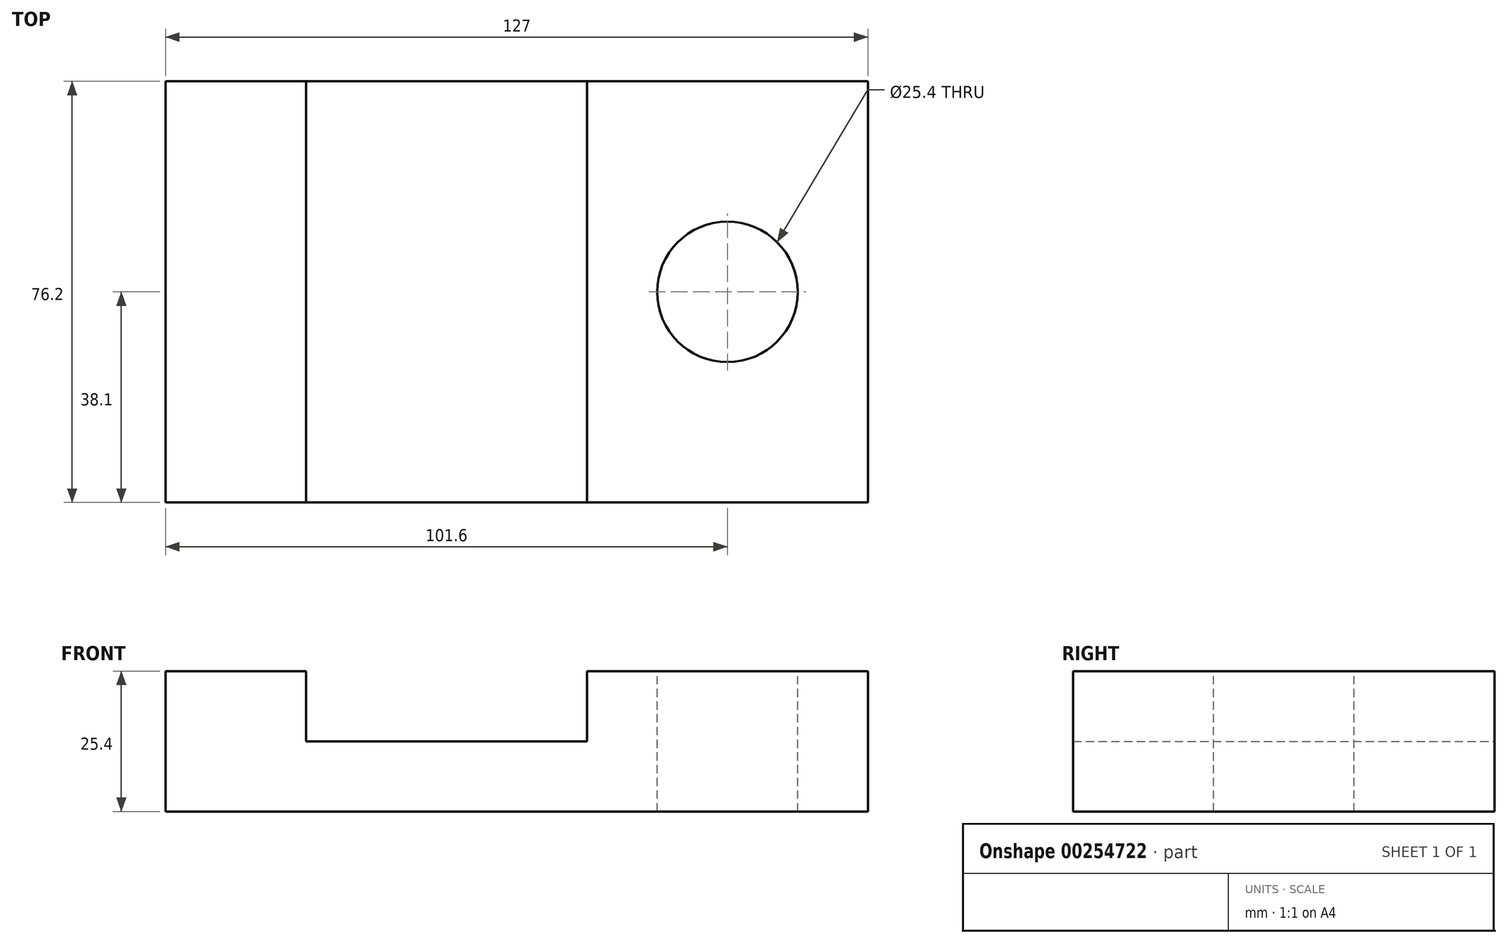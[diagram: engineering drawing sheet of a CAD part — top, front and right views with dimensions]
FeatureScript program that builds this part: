
annotation { "Feature Type Name" : "Feature", "Feature Type Description" : "" }
export const myFeature = defineFeature(function(context is Context, id is Id, definition is map)
    precondition{}
    {
        {
            var Q0;
            Q0=qCreatedBy(makeId("Top.planeOp"),FACE);
            var sketch = newSketch(context, id + "F0", { "sketchPlane" : qUnion([Q0])});
            skLineSegment(sketch, "E0", {"start": v(0, 0) * mm, "end": v(127, 0) * mm});
            skLineSegment(sketch, "E1", {"start": v(127, 0) * mm, "end": v(127, 76.2) * mm});
            skLineSegment(sketch, "E2", {"start": v(127, 76.2) * mm, "end": v(0, 76.2) * mm});
            skLineSegment(sketch, "E3", {"start": v(0, 76.2) * mm, "end": v(0, 0) * mm});
            skSolve(sketch);
        }
        {
            var Q0;
            Q0=makeQuery(id+"F0.imprint","IMPRINT",FACE,{"disambiguationData":[TD([[makeQuery(id+"F0.imprint","IMPRINT",EDGE,{"derivedFrom":sQuery(id+"F0.wireOp",EDGE,"E0")}),1.0]])]});
            extrude(context, id + "F1", {"entities" : qUnion([Q0]), "depth" : 25.4 * mm});
        }
        {
            var Q0;
            Q0=makeQuery(id+"F1.opExtrude","CAP_FACE",FACE,{"disambiguationData":[OSD([sQuery(id+"F0.wireOp",EDGE,"E0"),sQuery(id+"F0.wireOp",EDGE,"E1"),sQuery(id+"F0.wireOp",EDGE,"E2"),sQuery(id+"F0.wireOp",EDGE,"E3")])],"isStart":false});
            var sketch = newSketch(context, id + "F2", { "sketchPlane" : qUnion([Q0])});
            skLineSegment(sketch, "E4", {"start": v(0, 0) * mm, "end": v(25.4, 0) * mm});
            skLineSegment(sketch, "E5", {"start": v(25.4, 0) * mm, "end": v(25.4, 67.07) * mm});
            skLineSegment(sketch, "E6", {"start": v(25.4, 67.07) * mm, "end": v(25.4, 73.07) * mm});
            skLineSegment(sketch, "E7", {"start": v(25.4, 74.53) * mm, "end": v(25.4, 76.2) * mm});
            skLineSegment(sketch, "E8", {"start": v(25.4, 76.2) * mm, "end": v(25.4, 70.07) * mm});
            skLineSegment(sketch, "E9", {"start": v(127, 24.55) * mm, "end": v(76.2, 24.55) * mm});
            skLineSegment(sketch, "E10", {"start": v(76.2, 24.55) * mm, "end": v(76.2, 76.2) * mm});
            skLineSegment(sketch, "E11", {"start": v(76.2, 24.55) * mm, "end": v(76.2, 0) * mm});
            skCircle(sketch, "E12", {"center": v(101.6, 38.1) * mm, "radius": 12.7 * mm});
            skSolve(sketch);
        }
        {
            var Q0;
            Q0=qSketchRegion(id+"F2",true);
            var Q1;
            {var subQ7=sQuery(id+"F2.wireOp",EDGE,"E5");Q1=makeQuery(id+"F2.imprint","IMPRINT",FACE,{"disambiguationData":[TD([[makeQuery(id+"F2.imprint","IMPRINT",EDGE,{"derivedFrom":subQ7}),-1.0]])]});}
            extrude(context, id + "F3", {"entities" : qUnion([Q0, Q1]), "operationType" : NewBodyOperationType.REMOVE, "oppositeDirection" : true, "depth" : 12.7 * mm});
        }
        {
            var Q0;
            Q0=makeQuery(id+"F2.imprint","IMPRINT",FACE,{"disambiguationData":[TD([[makeQuery(id+"F2.imprint","IMPRINT",EDGE,{"derivedFrom":sQuery(id+"F2.wireOp",EDGE,"E12")}),1.0]])]});
            extrude(context, id + "F4", {"entities" : qUnion([Q0]), "operationType" : NewBodyOperationType.REMOVE, "oppositeDirection" : true, "depth" : 25.4 * mm});
        }
    });
